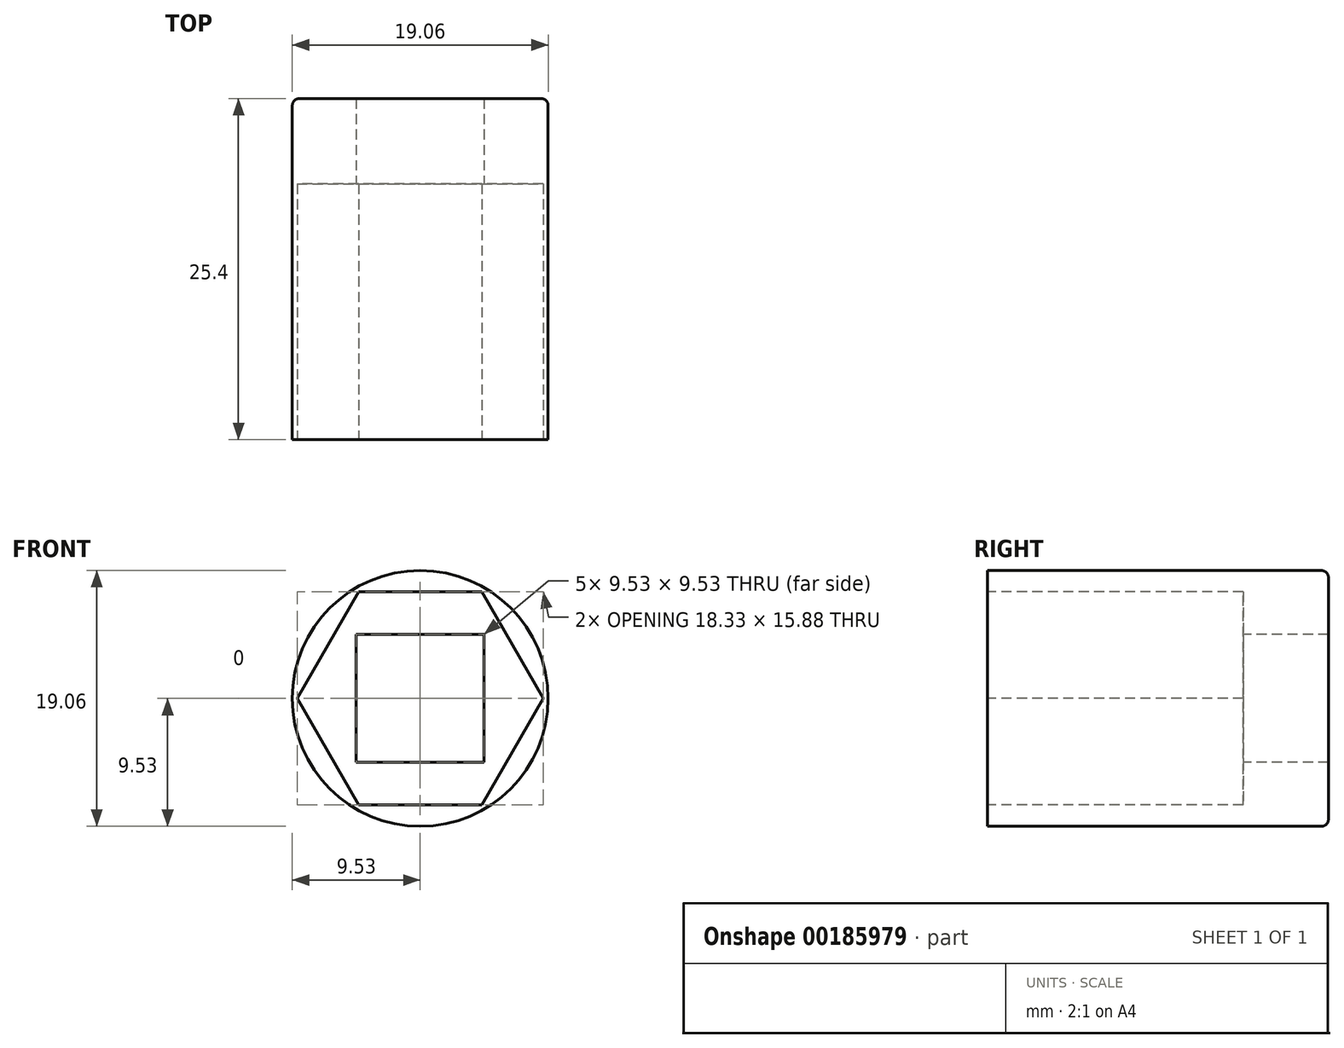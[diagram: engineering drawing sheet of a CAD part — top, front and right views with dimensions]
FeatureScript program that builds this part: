
annotation { "Feature Type Name" : "Feature", "Feature Type Description" : "" }
export const myFeature = defineFeature(function(context is Context, id is Id, definition is map)
    precondition{}
    {
        {
            var Q0;
            Q0=qCreatedBy(makeId("Front.planeOp"),FACE);
            var sketch = newSketch(context, id + "F0", { "sketchPlane" : qUnion([Q0])});
            skCircle(sketch, "E0", {"center": v(0, 0) * mm, "radius": 9.53 * mm});
            skSolve(sketch);
        }
        {
            var Q0;
            Q0 = qSketchRegion(id + "F0", true);
            extrude(context, id + "F1", {"entities" : qUnion([Q0]), "depth" : 25.4 * mm});
        }
        {
            var Q0;
            Q0=makeQuery(id+"F1.opExtrude","CAP_FACE",FACE,{"disambiguationData":[OSD([sQuery(id+"F0.wireOp",EDGE,"E0")])],"isStart":false});
            var sketch = newSketch(context, id + "F2", { "sketchPlane" : qUnion([Q0])});
            skLineSegment(sketch, "E1.bottom", {"start": v(4.76, -4.76) * mm, "end": v(-4.76, -4.76) * mm});
            skLineSegment(sketch, "E1.top", {"start": v(4.76, 4.76) * mm, "end": v(-4.76, 4.76) * mm});
            skLineSegment(sketch, "E1.left", {"start": v(4.76, -4.76) * mm, "end": v(4.76, 4.76) * mm});
            skLineSegment(sketch, "E1.right", {"start": v(-4.76, -4.76) * mm, "end": v(-4.76, 4.76) * mm});
            skPoint(sketch, "E1.middle", {"position": v(0, 0) * mm});
            skSolve(sketch);
        }
        {
            var Q0;
            Q0 = qSketchRegion(id + "F2", true);
            extrude(context, id + "F3", {"entities" : qUnion([Q0]), "operationType" : NewBodyOperationType.REMOVE, "endBound" : BoundingType.THROUGH_ALL, "oppositeDirection" : true, "depth" : 12.7 * mm});
        }
        {
            var Q0;
            Q0=makeQuery(id+"F1.opExtrude","CAP_FACE",FACE,{"disambiguationData":[OSD([sQuery(id+"F0.wireOp",EDGE,"E0")])],"isStart":false});
            var sketch = newSketch(context, id + "F4", { "sketchPlane" : qUnion([Q0])});
            skCircle(sketch, "E2.cCircle", {"center": v(0, 0) * mm, "radius": 7.94 * mm, "construction": true});
            skLineSegment(sketch, "E2.0", {"start": v(9.17, 0) * mm, "end": v(4.58, -7.94) * mm});
            skLineSegment(sketch, "E2.1", {"start": v(4.58, -7.94) * mm, "end": v(-4.59, -7.93) * mm});
            skLineSegment(sketch, "E2.2", {"start": v(-4.59, -7.93) * mm, "end": v(-9.17, 0) * mm});
            skLineSegment(sketch, "E2.3", {"start": v(-9.17, 0) * mm, "end": v(-4.58, 7.94) * mm});
            skLineSegment(sketch, "E2.4", {"start": v(-4.58, 7.94) * mm, "end": v(4.59, 7.93) * mm});
            skLineSegment(sketch, "E2.5", {"start": v(4.59, 7.93) * mm, "end": v(9.17, 0) * mm});
            skPoint(sketch, "E2.0.midPoint", {"position": v(6.87, -3.97) * mm});
            skSolve(sketch);
        }
        {
            var Q0;
            Q0 = qSketchRegion(id + "F4", true);
            extrude(context, id + "F5", {"entities" : qUnion([Q0]), "operationType" : NewBodyOperationType.REMOVE, "oppositeDirection" : true, "depth" : 19.05 * mm});
        }
        {
            var Q0;
            Q0=makeQuery(id+"F1.opExtrude","CAP_EDGE",EDGE,{"disambiguationData":[OSD([sQuery(id+"F0.wireOp",EDGE,"E0")])],"isStart":true});
            fillet(context, id + "F6", {"entities" : qUnion([Q0]), "radius" : 0.5 * mm, "tangentPropagation" : true, "allowEdgeOverflow" : false});
        }
    });
